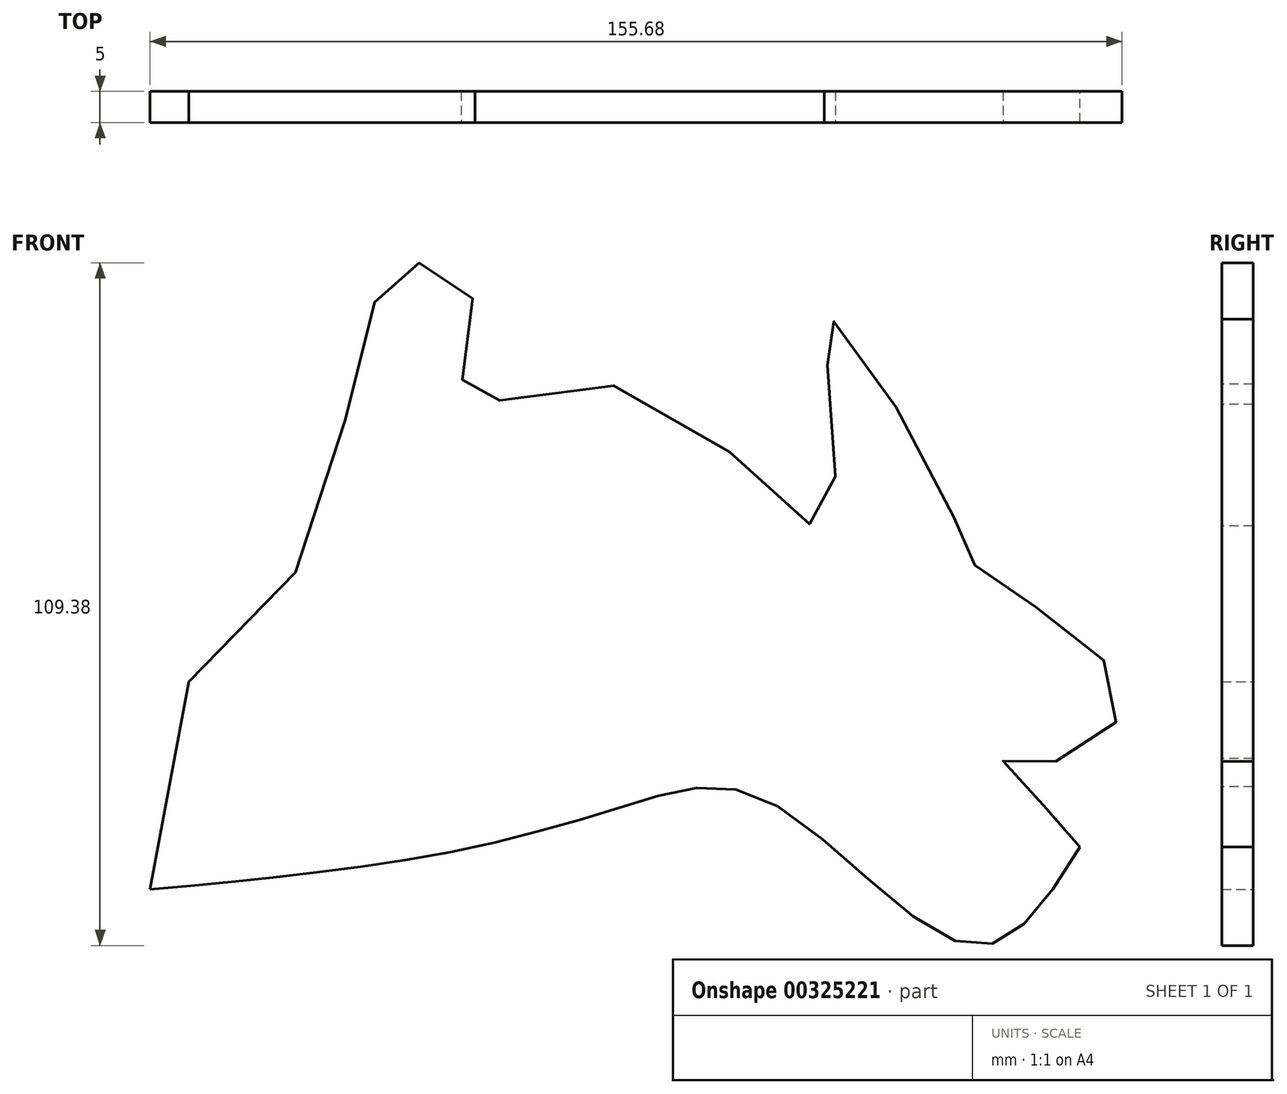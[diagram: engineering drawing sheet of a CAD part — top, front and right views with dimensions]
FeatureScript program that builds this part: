
annotation { "Feature Type Name" : "Feature", "Feature Type Description" : "" }
export const myFeature = defineFeature(function(context is Context, id is Id, definition is map)
    precondition{}
    {
        {
            var Q0;
            Q0=qCreatedBy(makeId("Front.planeOp"),FACE);
            var sketch = newSketch(context, id + "F0", { "sketchPlane" : qUnion([Q0])});
            skFitSpline(sketch, "E0", {"points": [v(-71.02, 12.57) * mm, v(-42.88, 68.35) * mm, v(-34.92, 79.65) * mm, v(-25.38, 73.36) * mm, v(-27, 57.67) * mm, v(0, 59.44) * mm, v(29.93, 37.53) * mm, v(31.64, 60.03) * mm, v(31.75, 70.64) * mm, v(51.19, 39.7) * mm, v(54.52, 31.65) * mm, v(68.4, 22.05) * mm, v(78.42, 9.4) * mm, v(69.02, 0) * mm, v(59.4, 0) * mm, v(65.75, -7.15) * mm, v(71.68, -13.9) * mm], "startDerivative": vector(544.84, 228.92) * mm, "endDerivative": vector(106.08, -133.84) * mm});
            skFitSpline(sketch, "E1", {"points": [v(71.68, -13.9) * mm, v(54.38, -29.64) * mm, v(21.57, -6.43) * mm, v(0, -6.97) * mm, v(-25.24, -13.9) * mm, v(-53.24, -18.3) * mm, v(-77.25, -20.7) * mm], "startDerivative": vector(-98.33, -160.33) * mm, "endDerivative": vector(-148.95, -13.6) * mm});
            skLineSegment(sketch, "E2", {"start": v(-77.25, -20.7) * mm, "end": v(-71.02, 12.57) * mm});
            skSolve(sketch);
        }
        {
            var Q0;
            Q0=makeQuery(id+"F0.imprint","IMPRINT",FACE,{"disambiguationData":[TD([[makeQuery(id+"F0.imprint","IMPRINT",EDGE,{"derivedFrom":sQuery(id+"F0.wireOp",EDGE,"E0")}),-1.0]])]});
            extrude(context, id + "F1", {"entities" : qUnion([Q0]), "depth" : 5 * mm});
        }
    });
